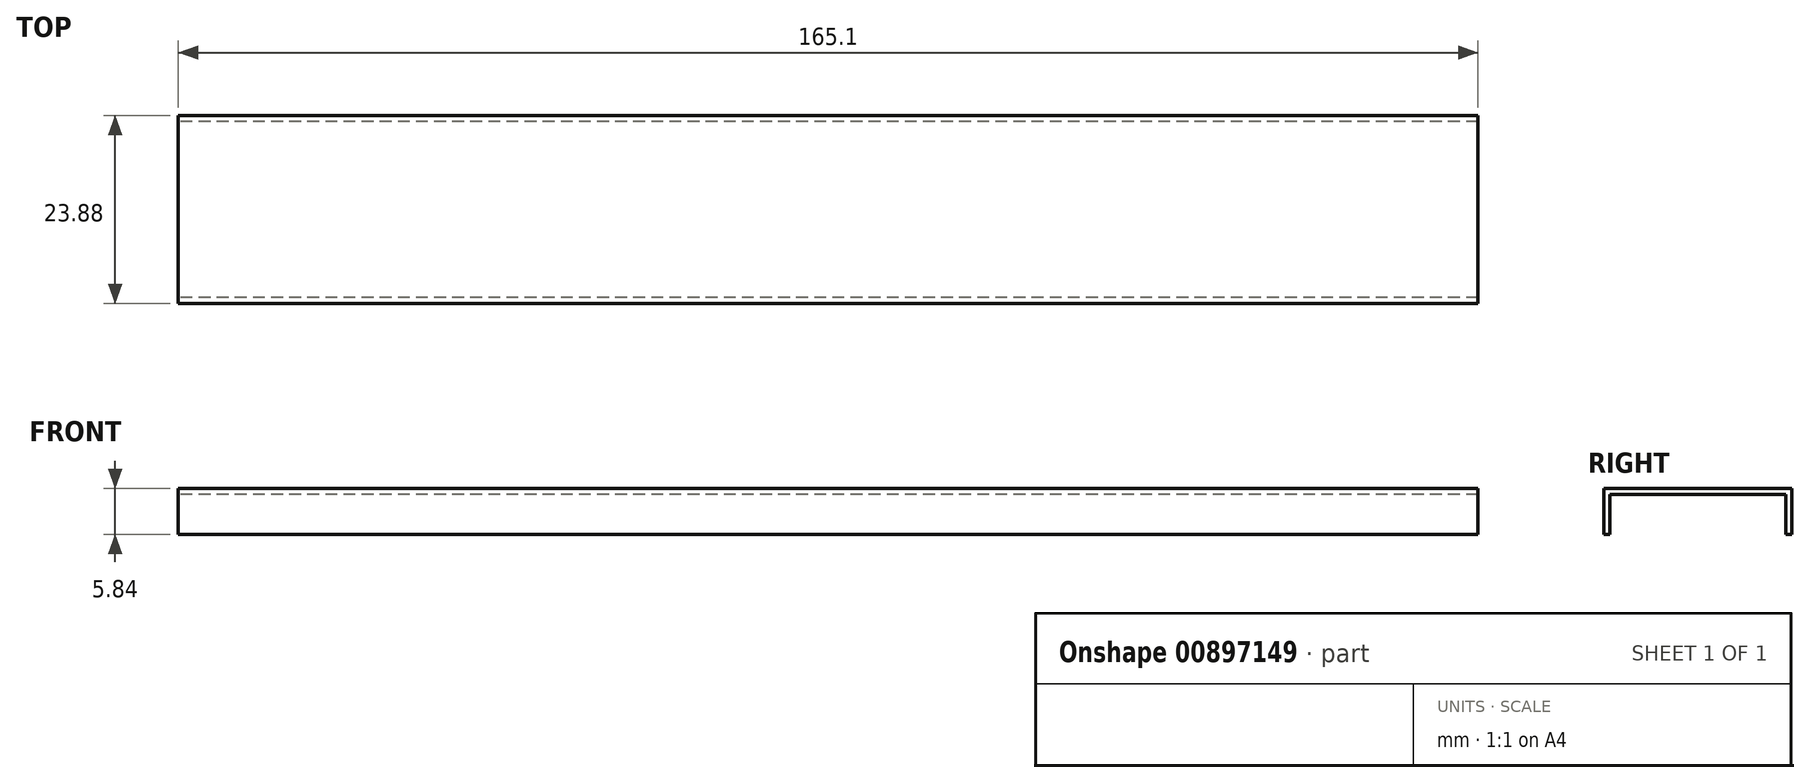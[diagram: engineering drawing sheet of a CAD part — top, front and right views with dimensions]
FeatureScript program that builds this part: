
annotation { "Feature Type Name" : "Feature", "Feature Type Description" : "" }
export const myFeature = defineFeature(function(context is Context, id is Id, definition is map)
    precondition{}
    {
        {
            var Q0;
            Q0=qCreatedBy(makeId("Right.planeOp"),FACE);
            var sketch = newSketch(context, id + "F0", { "sketchPlane" : qUnion([Q0])});
            skLineSegment(sketch, "E0", {"start": v(0, 0) * mm, "end": v(0, 5.84) * mm});
            skLineSegment(sketch, "E1", {"start": v(0, 5.84) * mm, "end": v(23.88, 5.84) * mm});
            skLineSegment(sketch, "E2", {"start": v(23.88, 5.84) * mm, "end": v(23.88, 0) * mm});
            skLineSegment(sketch, "E3", {"start": v(23.88, 0) * mm, "end": v(23.11, 0) * mm});
            skLineSegment(sketch, "E4", {"start": v(23.11, 0) * mm, "end": v(23.11, 5.08) * mm});
            skLineSegment(sketch, "E5", {"start": v(23.11, 5.08) * mm, "end": v(0.76, 5.08) * mm});
            skLineSegment(sketch, "E6", {"start": v(0.76, 5.08) * mm, "end": v(0.76, 0) * mm});
            skLineSegment(sketch, "E7", {"start": v(0.76, 0) * mm, "end": v(0, 0) * mm});
            skLineSegment(sketch, "E8", {"start": v(11.94, 5.08) * mm, "end": v(11.94, 5.84) * mm, "construction": true});
            skSolve(sketch);
        }
        {
            var Q0;
            Q0 = qSketchRegion(id + "F0", true);
            extrude(context, id + "F1", {"entities" : qUnion([Q0]), "depth" : 165.1 * mm, "offsetDistance" : 25.4 * mm});
        }
    });
